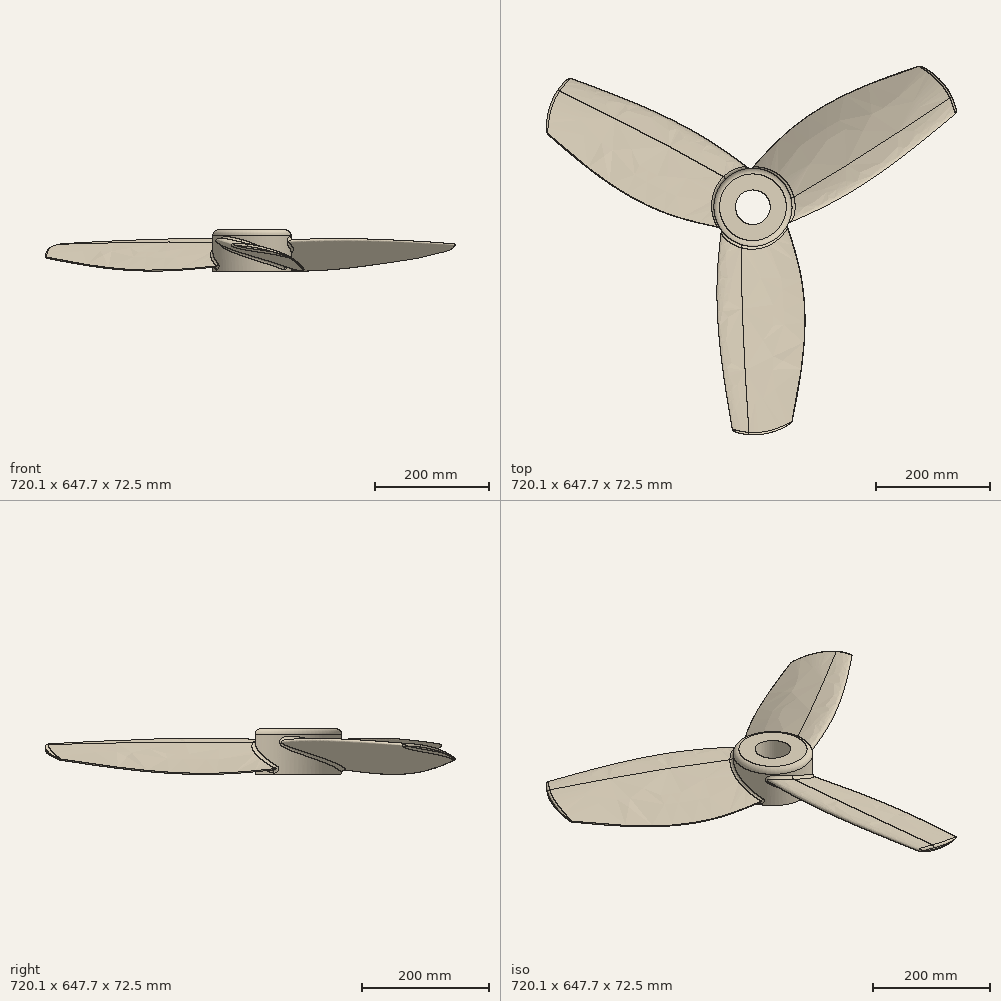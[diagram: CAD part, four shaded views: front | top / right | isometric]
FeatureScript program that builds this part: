
annotation { "Feature Type Name" : "Feature", "Feature Type Description" : "" }
export const myFeature = defineFeature(function(context is Context, id is Id, definition is map)
    precondition{}
    {
        {
            var Q0;
            Q0=qCreatedBy(makeId("Front.planeOp"),FACE);
            var sketch = newSketch(context, id + "F0", { "sketchPlane" : qUnion([Q0])});
            skLineSegment(sketch, "E0", {"start": v(-25.68, 10.16) * mm, "end": v(0, 0) * mm, "construction": true});
            skLineSegment(sketch, "E1", {"start": v(0, 0) * mm, "end": v(25.68, -10.16) * mm, "construction": true});
            skLineSegment(sketch, "E2", {"start": v(25.68, -10.16) * mm, "end": v(51.36, -20.31) * mm, "construction": true});
            skLineSegment(sketch, "E3", {"start": v(51.36, -20.31) * mm, "end": v(77.03, -30.47) * mm, "construction": true});
            skLineSegment(sketch, "E4", {"start": v(0, 0) * mm, "end": v(3.73, 9.44) * mm, "construction": true});
            skLineSegment(sketch, "E5", {"start": v(-25.68, 10.16) * mm, "end": v(-23.81, 14.88) * mm, "construction": true});
            skFitSpline(sketch, "E6", {"points": [v(-25.68, 10.16) * mm, v(3.73, 9.44) * mm, v(77.03, -30.47) * mm], "startDerivative": vector(15.03, 38) * mm, "endDerivative": vector(104.92, -93.69) * mm});
            skPoint(sketch, "E7", {"position": v(1.87, 4.72) * mm});
            skLineSegment(sketch, "E8", {"start": v(-23.81, 14.88) * mm, "end": v(1.87, 4.72) * mm, "construction": true});
            skLineSegment(sketch, "E9", {"start": v(0, 0) * mm, "end": v(-1.87, -4.72) * mm, "construction": true});
            skLineSegment(sketch, "E10", {"start": v(-25.68, 10.16) * mm, "end": v(-27.54, 5.44) * mm, "construction": true});
            skFitSpline(sketch, "E11", {"points": [v(-25.68, 10.16) * mm, v(-1.87, -4.72) * mm, v(77.03, -30.47) * mm], "startDerivative": vector(-15.23, -38.5) * mm, "endDerivative": vector(121.84, -48.19) * mm});
            skLineSegment(sketch, "E12", {"start": v(51.36, -20.31) * mm, "end": v(55.09, -10.87) * mm, "construction": true});
            skSolve(sketch);
        }
        {
            var Q0;
            Q0=qCreatedBy(makeId("Front.planeOp"),FACE);
            cPlane(context, id + "F1", {"entities" : qUnion([Q0]), "cplaneType" : CPlaneType.OFFSET, "offset" : 125 * mm, "width" : 150 * mm, "height" : 150 * mm});
        }
        {
            var Q0;
            Q0=qCreatedBy(id+"F1.planeOp",FACE);
            var sketch = newSketch(context, id + "F2", { "sketchPlane" : qUnion([Q0])});
            skLineSegment(sketch, "E13", {"start": v(-38.33, 14.06) * mm, "end": v(0, 0) * mm, "construction": true});
            skLineSegment(sketch, "E14", {"start": v(0, 0) * mm, "end": v(38.33, -14.06) * mm, "construction": true});
            skLineSegment(sketch, "E15", {"start": v(38.33, -14.06) * mm, "end": v(76.67, -28.12) * mm, "construction": true});
            skLineSegment(sketch, "E16", {"start": v(76.67, -28.12) * mm, "end": v(115, -42.17) * mm, "construction": true});
            skLineSegment(sketch, "E17", {"start": v(0, 0) * mm, "end": v(4.06, 11.06) * mm, "construction": true});
            skLineSegment(sketch, "E18", {"start": v(-38.33, 14.06) * mm, "end": v(-36.3, 19.59) * mm, "construction": true});
            skFitSpline(sketch, "E19", {"points": [v(-38.33, 14.06) * mm, v(4.06, 11.06) * mm, v(115, -42.17) * mm], "startDerivative": vector(16.44, 44.82) * mm, "endDerivative": vector(163.27, -119.63) * mm});
            skPoint(sketch, "E20", {"position": v(2.03, 5.53) * mm});
            skLineSegment(sketch, "E21", {"start": v(-36.3, 19.59) * mm, "end": v(2.03, 5.53) * mm, "construction": true});
            skLineSegment(sketch, "E22", {"start": v(0, 0) * mm, "end": v(-2.03, -5.53) * mm, "construction": true});
            skLineSegment(sketch, "E23", {"start": v(-38.33, 14.06) * mm, "end": v(-40.36, 8.53) * mm, "construction": true});
            skFitSpline(sketch, "E24", {"points": [v(-38.33, 14.06) * mm, v(-2.03, -5.53) * mm, v(115, -42.17) * mm], "startDerivative": vector(-16.57, -45.19) * mm, "endDerivative": vector(181.7, -66.64) * mm});
            skLineSegment(sketch, "E25", {"start": v(76.67, -28.12) * mm, "end": v(80.72, -17.06) * mm, "construction": true});
            skSolve(sketch);
        }
        {
            var Q0;
            Q0=qCreatedBy(makeId("Front.planeOp"),FACE);
            cPlane(context, id + "F3", {"entities" : qUnion([Q0]), "cplaneType" : CPlaneType.OFFSET, "offset" : 400 * mm, "width" : 150 * mm, "height" : 150 * mm});
        }
        {
            var Q0;
            Q0=qCreatedBy(id+"F3.planeOp",FACE);
            var sketch = newSketch(context, id + "F4", { "sketchPlane" : qUnion([Q0])});
            skLineSegment(sketch, "E26", {"start": v(-10.03, 5.14) * mm, "end": v(16.27, 0) * mm, "construction": true});
            skLineSegment(sketch, "E27", {"start": v(16.27, 0) * mm, "end": v(42.56, -5.14) * mm, "construction": true});
            skLineSegment(sketch, "E28", {"start": v(42.56, -5.14) * mm, "end": v(68.86, -10.28) * mm, "construction": true});
            skLineSegment(sketch, "E29", {"start": v(68.86, -10.28) * mm, "end": v(95.16, -15.42) * mm, "construction": true});
            skLineSegment(sketch, "E30", {"start": v(16.27, 0) * mm, "end": v(17.61, 6.9) * mm, "construction": true});
            skLineSegment(sketch, "E31", {"start": v(-10.03, 5.14) * mm, "end": v(-9.36, 8.59) * mm, "construction": true});
            skFitSpline(sketch, "E32", {"points": [v(-10.03, 5.14) * mm, v(17.61, 6.9) * mm, v(95.16, -15.42) * mm], "startDerivative": vector(5.47, 28.01) * mm, "endDerivative": vector(118.7, -57.28) * mm});
            skPoint(sketch, "E33", {"position": v(16.94, 3.45) * mm});
            skLineSegment(sketch, "E34", {"start": v(-9.36, 8.59) * mm, "end": v(16.94, 3.45) * mm, "construction": true});
            skLineSegment(sketch, "E35", {"start": v(16.27, 0) * mm, "end": v(15.6, -3.45) * mm, "construction": true});
            skLineSegment(sketch, "E36", {"start": v(-10.03, 5.14) * mm, "end": v(-10.7, 1.7) * mm, "construction": true});
            skFitSpline(sketch, "E37", {"points": [v(-10.03, 5.14) * mm, v(15.6, -3.45) * mm, v(95.16, -15.42) * mm], "startDerivative": vector(-5.51, -28.2) * mm, "endDerivative": vector(124.61, -24.36) * mm});
            skLineSegment(sketch, "E38", {"start": v(68.86, -10.28) * mm, "end": v(70.2, -3.38) * mm, "construction": true});
            skSolve(sketch);
        }
        {
            var Q0;
            Q0=qSketchRegion(id+"F0",true);
            var Q1;
            Q1=qSketchRegion(id+"F2",true);
            var Q2;
            Q2=qSketchRegion(id+"F4",true);
            var Q3;
            Q3=sQuery(id+"F0.wireOp",VERTEX,"E6.1.internal");
            var Q4;
            Q4=sQuery(id+"F2.wireOp",VERTEX,"E19.1.internal");
            var Q5;
            Q5=sQuery(id+"F4.wireOp",VERTEX,"E30.end");
            loft(context, id + "F5", {"sheetProfilesArray" : [{ "sheetProfileEntities" : qUnion([Q0]) }, { "sheetProfileEntities" : qUnion([Q1]) }, { "sheetProfileEntities" : qUnion([Q2]) }], "matchConnections" : true, "connections" : [{ "connectionEntities" : qUnion([Q3, Q4, Q5]), "connectionEdgeQueries" : qUnion([]), "connectionEdgeParameters" : [] }]});
        }
        {
            var Q0;
            Q0=qCreatedBy(makeId("Top.planeOp"),FACE);
            var sketch = newSketch(context, id + "F6", { "sketchPlane" : qUnion([Q0])});
            skFitSpline(sketch, "E39", {"points": [v(-55.98, -360.47) * mm, v(39.38, -398.87) * mm, v(142.8, -333.19) * mm], "startDerivative": vector(111.22, -150.8) * mm, "endDerivative": vector(54.24, 145.78) * mm});
            skLineSegment(sketch, "E40", {"start": v(-55.98, -360.47) * mm, "end": v(-55.98, -458.75) * mm});
            skLineSegment(sketch, "E41", {"start": v(142.8, -333.19) * mm, "end": v(142.8, -458.75) * mm});
            skLineSegment(sketch, "E42", {"start": v(142.8, -458.75) * mm, "end": v(-55.98, -458.75) * mm});
            skSolve(sketch);
        }
        {
            var Q0;
            Q0=qSketchRegion(id+"F6",true);
            extrude(context, id + "F7", {"entities" : qUnion([Q0]), "operationType" : NewBodyOperationType.REMOVE, "endBound" : BoundingType.SYMMETRIC, "oppositeDirection" : true, "depth" : 40.17 * mm, "offsetDistance" : 25 * mm});
        }
        {
            var Q0;
            Q0=makeQuery(id+"F5.opLoft","SWEPT_EDGE",EDGE,{"disambiguationData":[OSD([sQuery(id+"F2.wireOp",EDGE,"E19"),sQuery(id+"F2.wireOp",EDGE,"E24"),sQuery(id+"F4.wireOp",EDGE,"E32"),sQuery(id+"F4.wireOp",EDGE,"E37")])]});
            fillet(context, id + "F8", {"entities" : qUnion([Q0]), "radius" : 1 * mm, "tangentPropagation" : true, "allowEdgeOverflow" : false});
        }
        {
            var Q0;
            Q0=makeQuery(id+"F7.boolean.opBoolean","COPY",FACE,{"derivedFrom":makeQuery(id+"F7.opExtrude","SWEPT_FACE",FACE,{"disambiguationData":[OSD([sQuery(id+"F6.wireOp",EDGE,"E39")])]})});
            fillet(context, id + "F9", {"entities" : qUnion([Q0]), "radius" : 4 * mm, "tangentPropagation" : true, "allowEdgeOverflow" : false});
        }
        {
            var Q0;
            Q0=qCreatedBy(makeId("Top.planeOp"),FACE);
            var sketch = newSketch(context, id + "F10", { "sketchPlane" : qUnion([Q0])});
            skCircle(sketch, "E43", {"center": v(24.35, 0) * mm, "radius": 68.6 * mm});
            skSolve(sketch);
        }
        {
            var Q0;
            Q0=qSketchRegion(id+"F10",true);
            extrude(context, id + "F11", {"entities" : qUnion([Q0]), "depth" : 32.31 * mm, "hasSecondDirection" : true, "secondDirectionOppositeDirection" : true, "secondDirectionDepth" : 40 * mm});
        }
        {
            var Q0;
            Q0=makeQuery(id+"F5.opLoft","SWEPT_BODY",BODY,{"disambiguationData":[OSD([makeQuery(id+"F0.imprint","IMPRINT",FACE,{"disambiguationData":[TD([[makeQuery(id+"F0.imprint","IMPRINT",EDGE,{"derivedFrom":sQuery(id+"F0.wireOp",EDGE,"E6")}),-1.0]])]}),sQuery(id+"F2.wireOp",EDGE,"E24"),makeQuery(id+"F4.imprint","IMPRINT",FACE,{"disambiguationData":[TD([[makeQuery(id+"F4.imprint","IMPRINT",EDGE,{"derivedFrom":sQuery(id+"F4.wireOp",EDGE,"E32")}),-1.0]])]})])]});
            var Q1;
            Q1=makeQuery(id+"F11.opExtrude","SWEPT_FACE",FACE,{"disambiguationData":[OSD([sQuery(id+"F10.wireOp",EDGE,"E43")])]});
            circularPattern(context, id + "F12", {"entities" : qUnion([Q0]), "axis" : qUnion([Q1]), "angle" : 360 * degree, "instanceCount" : 3, "equalSpace" : true});
        }
        {
            var Q0;
            Q0=makeQuery(id+"F12.opPattern","COPY",BODY,{"derivedFrom":makeQuery(id+"F5.opLoft","SWEPT_BODY",BODY,{"disambiguationData":[OSD([makeQuery(id+"F0.imprint","IMPRINT",FACE,{"disambiguationData":[TD([[makeQuery(id+"F0.imprint","IMPRINT",EDGE,{"derivedFrom":sQuery(id+"F0.wireOp",EDGE,"E6")}),-1.0]])]}),sQuery(id+"F2.wireOp",EDGE,"E24"),makeQuery(id+"F4.imprint","IMPRINT",FACE,{"disambiguationData":[TD([[makeQuery(id+"F4.imprint","IMPRINT",EDGE,{"derivedFrom":sQuery(id+"F4.wireOp",EDGE,"E32")}),-1.0]])]})])]}),"instanceName":"2"});
            var Q1;
            Q1=makeQuery(id+"F5.opLoft","SWEPT_BODY",BODY,{"disambiguationData":[OSD([makeQuery(id+"F0.imprint","IMPRINT",FACE,{"disambiguationData":[TD([[makeQuery(id+"F0.imprint","IMPRINT",EDGE,{"derivedFrom":sQuery(id+"F0.wireOp",EDGE,"E6")}),-1.0]])]}),sQuery(id+"F2.wireOp",EDGE,"E24"),makeQuery(id+"F4.imprint","IMPRINT",FACE,{"disambiguationData":[TD([[makeQuery(id+"F4.imprint","IMPRINT",EDGE,{"derivedFrom":sQuery(id+"F4.wireOp",EDGE,"E32")}),-1.0]])]})])]});
            var Q2;
            Q2=makeQuery(id+"F11.opExtrude","SWEPT_BODY",BODY,{"disambiguationData":[OSD([sQuery(id+"F10.wireOp",EDGE,"E43")])]});
            var Q3;
            Q3=makeQuery(id+"F12.opPattern","COPY",BODY,{"derivedFrom":makeQuery(id+"F5.opLoft","SWEPT_BODY",BODY,{"disambiguationData":[OSD([makeQuery(id+"F0.imprint","IMPRINT",FACE,{"disambiguationData":[TD([[makeQuery(id+"F0.imprint","IMPRINT",EDGE,{"derivedFrom":sQuery(id+"F0.wireOp",EDGE,"E6")}),-1.0]])]}),sQuery(id+"F2.wireOp",EDGE,"E24"),makeQuery(id+"F4.imprint","IMPRINT",FACE,{"disambiguationData":[TD([[makeQuery(id+"F4.imprint","IMPRINT",EDGE,{"derivedFrom":sQuery(id+"F4.wireOp",EDGE,"E32")}),-1.0]])]})])]}),"instanceName":"1"});
            var Q4;
            Q4=makeQuery(id+"F12.opPattern","COPY",BODY,{"derivedFrom":makeQuery(id+"F5.opLoft","SWEPT_BODY",BODY,{"disambiguationData":[OSD([makeQuery(id+"F0.imprint","IMPRINT",FACE,{"disambiguationData":[TD([[makeQuery(id+"F0.imprint","IMPRINT",EDGE,{"derivedFrom":sQuery(id+"F0.wireOp",EDGE,"E6")}),-1.0]])]}),sQuery(id+"F2.wireOp",EDGE,"E24"),makeQuery(id+"F4.imprint","IMPRINT",FACE,{"disambiguationData":[TD([[makeQuery(id+"F4.imprint","IMPRINT",EDGE,{"derivedFrom":sQuery(id+"F4.wireOp",EDGE,"E32")}),-1.0]])]})])]}),"instanceName":"4"});
            var Q5;
            Q5=makeQuery(id+"F12.opPattern","COPY",BODY,{"derivedFrom":makeQuery(id+"F5.opLoft","SWEPT_BODY",BODY,{"disambiguationData":[OSD([makeQuery(id+"F0.imprint","IMPRINT",FACE,{"disambiguationData":[TD([[makeQuery(id+"F0.imprint","IMPRINT",EDGE,{"derivedFrom":sQuery(id+"F0.wireOp",EDGE,"E6")}),-1.0]])]}),sQuery(id+"F2.wireOp",EDGE,"E24"),makeQuery(id+"F4.imprint","IMPRINT",FACE,{"disambiguationData":[TD([[makeQuery(id+"F4.imprint","IMPRINT",EDGE,{"derivedFrom":sQuery(id+"F4.wireOp",EDGE,"E32")}),-1.0]])]})])]}),"instanceName":"3"});
            booleanBodies(context, id + "F13", {"operationType" : BooleanOperationType.UNION, "tools" : qUnion([Q0, Q1, Q2, Q3, Q4, Q5])});
        }
        {
            var Q0;
            Q0=makeQuery(id+"F11.opExtrude","CAP_FACE",FACE,{"disambiguationData":[OSD([sQuery(id+"F10.wireOp",EDGE,"E43")])],"isStart":false});
            var sketch = newSketch(context, id + "F14", { "sketchPlane" : qUnion([Q0])});
            skCircle(sketch, "E44", {"center": v(24.35, 0) * mm, "radius": 30.45 * mm});
            skSolve(sketch);
        }
        {
            var Q0;
            Q0=qSketchRegion(id+"F14",true);
            var Q1;
            Q1 = qSketchRegion(id + "F14", true);
            var Q2;
            Q2 = qSketchRegion(id + "F14", true);
            extrude(context, id + "F15", {"entities" : qUnion([Q0, Q1, Q2]), "operationType" : NewBodyOperationType.REMOVE, "endBound" : BoundingType.THROUGH_ALL, "oppositeDirection" : true, "depth" : 25 * mm, "offsetDistance" : 25 * mm});
        }
        {
            var Q0;
            {var subQ0=sQuery(id+"F0.wireOp",VERTEX,"E6.1.internal");var subQ1=sQuery(id+"F0.wireOp",EDGE,"E6");var subQ2=sQuery(id+"F0.wireOp",EDGE,"E11");var subQ3=sQuery(id+"F2.wireOp",VERTEX,"E19.1.internal");var subQ4=sQuery(id+"F2.wireOp",EDGE,"E19");var subQ5=sQuery(id+"F2.wireOp",EDGE,"E24");Q0=makeQuery(id+"F13.opBoolean","INTERSECT",EDGE,{"derivedFrom":[makeQuery(id+"F11.opExtrude","SWEPT_FACE",FACE,{"disambiguationData":[OSD([sQuery(id+"F10.wireOp",EDGE,"E43")])]}),makeQuery(id+"F12.opPattern","COPY",FACE,{"derivedFrom":makeQuery(id+"F5.opLoft","SWEPT_FACE",FACE,{"disambiguationData":[OSD([subQ0,subQ1,subQ2,subQ3,subQ4,subQ5]),TDD([subQ0,makeQuery(id+"F0.imprint","INTERSECT",VERTEX,{"disambiguationData":[OD(0.0)],"derivedFrom":[subQ1,subQ2]}),makeQuery(id+"F0.imprint","IMPRINT",EDGE,{"derivedFrom":subQ1}),subQ3,makeQuery(id+"F2.imprint","INTERSECT",VERTEX,{"disambiguationData":[OD(0.0)],"derivedFrom":[subQ4,subQ5]}),makeQuery(id+"F2.imprint","IMPRINT",EDGE,{"derivedFrom":subQ4})])]}),"instanceName":"2"})]});}
            var Q1;
            {var subQ0=sQuery(id+"F0.wireOp",VERTEX,"E6.1.internal");var subQ1=sQuery(id+"F0.wireOp",EDGE,"E6");var subQ2=sQuery(id+"F0.wireOp",EDGE,"E11");var subQ3=sQuery(id+"F2.wireOp",VERTEX,"E19.1.internal");var subQ4=sQuery(id+"F2.wireOp",EDGE,"E19");var subQ5=sQuery(id+"F2.wireOp",EDGE,"E24");Q1=makeQuery(id+"F13.opBoolean","INTERSECT",EDGE,{"derivedFrom":[makeQuery(id+"F5.opLoft","SWEPT_FACE",FACE,{"disambiguationData":[OSD([subQ0,subQ1,subQ2,subQ3,subQ4,subQ5]),TDD([subQ0,makeQuery(id+"F0.imprint","INTERSECT",VERTEX,{"disambiguationData":[OD(1.0)],"derivedFrom":[subQ1,subQ2]}),makeQuery(id+"F0.imprint","IMPRINT",EDGE,{"derivedFrom":subQ1}),subQ3,makeQuery(id+"F2.imprint","INTERSECT",VERTEX,{"disambiguationData":[OD(1.0)],"derivedFrom":[subQ4,subQ5]}),makeQuery(id+"F2.imprint","IMPRINT",EDGE,{"derivedFrom":subQ4})])]}),makeQuery(id+"F11.opExtrude","SWEPT_FACE",FACE,{"disambiguationData":[OSD([sQuery(id+"F10.wireOp",EDGE,"E43")])]})]});}
            var Q2;
            {var subQ0=sQuery(id+"F0.wireOp",VERTEX,"E6.1.internal");var subQ1=sQuery(id+"F0.wireOp",EDGE,"E6");var subQ2=sQuery(id+"F0.wireOp",EDGE,"E11");var subQ3=sQuery(id+"F2.wireOp",VERTEX,"E19.1.internal");var subQ4=sQuery(id+"F2.wireOp",EDGE,"E19");var subQ5=sQuery(id+"F2.wireOp",EDGE,"E24");Q2=makeQuery(id+"F13.opBoolean","INTERSECT",EDGE,{"derivedFrom":[makeQuery(id+"F11.opExtrude","SWEPT_FACE",FACE,{"disambiguationData":[OSD([sQuery(id+"F10.wireOp",EDGE,"E43")])]}),makeQuery(id+"F12.opPattern","COPY",FACE,{"derivedFrom":makeQuery(id+"F5.opLoft","SWEPT_FACE",FACE,{"disambiguationData":[OSD([subQ0,subQ1,subQ2,subQ3,subQ4,subQ5]),TDD([subQ0,makeQuery(id+"F0.imprint","INTERSECT",VERTEX,{"disambiguationData":[OD(1.0)],"derivedFrom":[subQ1,subQ2]}),makeQuery(id+"F0.imprint","IMPRINT",EDGE,{"derivedFrom":subQ1}),subQ3,makeQuery(id+"F2.imprint","INTERSECT",VERTEX,{"disambiguationData":[OD(1.0)],"derivedFrom":[subQ4,subQ5]}),makeQuery(id+"F2.imprint","IMPRINT",EDGE,{"derivedFrom":subQ4})])]}),"instanceName":"1"})]});}
            var Q3;
            {var subQ0=sQuery(id+"F0.wireOp",VERTEX,"E6.1.internal");var subQ1=sQuery(id+"F0.wireOp",EDGE,"E6");var subQ2=sQuery(id+"F0.wireOp",EDGE,"E11");var subQ3=sQuery(id+"F2.wireOp",VERTEX,"E19.1.internal");var subQ4=sQuery(id+"F2.wireOp",EDGE,"E19");var subQ5=sQuery(id+"F2.wireOp",EDGE,"E24");Q3=makeQuery(id+"F13.opBoolean","INTERSECT",EDGE,{"derivedFrom":[makeQuery(id+"F11.opExtrude","SWEPT_FACE",FACE,{"disambiguationData":[OSD([sQuery(id+"F10.wireOp",EDGE,"E43")])]}),makeQuery(id+"F12.opPattern","COPY",FACE,{"derivedFrom":makeQuery(id+"F5.opLoft","SWEPT_FACE",FACE,{"disambiguationData":[OSD([subQ0,subQ1,subQ2,subQ3,subQ4,subQ5]),TDD([subQ0,makeQuery(id+"F0.imprint","INTERSECT",VERTEX,{"disambiguationData":[OD(1.0)],"derivedFrom":[subQ1,subQ2]}),makeQuery(id+"F0.imprint","IMPRINT",EDGE,{"derivedFrom":subQ1}),subQ3,makeQuery(id+"F2.imprint","INTERSECT",VERTEX,{"disambiguationData":[OD(1.0)],"derivedFrom":[subQ4,subQ5]}),makeQuery(id+"F2.imprint","IMPRINT",EDGE,{"derivedFrom":subQ4})])]}),"instanceName":"4"})]});}
            var Q4;
            {var subQ0=sQuery(id+"F0.wireOp",VERTEX,"E6.1.internal");var subQ1=sQuery(id+"F0.wireOp",EDGE,"E6");var subQ2=sQuery(id+"F0.wireOp",EDGE,"E11");var subQ3=sQuery(id+"F2.wireOp",VERTEX,"E19.1.internal");var subQ4=sQuery(id+"F2.wireOp",EDGE,"E19");var subQ5=sQuery(id+"F2.wireOp",EDGE,"E24");Q4=makeQuery(id+"F13.opBoolean","INTERSECT",EDGE,{"derivedFrom":[makeQuery(id+"F11.opExtrude","SWEPT_FACE",FACE,{"disambiguationData":[OSD([sQuery(id+"F10.wireOp",EDGE,"E43")])]}),makeQuery(id+"F12.opPattern","COPY",FACE,{"derivedFrom":makeQuery(id+"F5.opLoft","SWEPT_FACE",FACE,{"disambiguationData":[OSD([subQ0,subQ1,subQ2,subQ3,subQ4,subQ5]),TDD([subQ0,makeQuery(id+"F0.imprint","INTERSECT",VERTEX,{"disambiguationData":[OD(0.0)],"derivedFrom":[subQ1,subQ2]}),makeQuery(id+"F0.imprint","IMPRINT",EDGE,{"derivedFrom":subQ1}),subQ3,makeQuery(id+"F2.imprint","INTERSECT",VERTEX,{"disambiguationData":[OD(0.0)],"derivedFrom":[subQ4,subQ5]}),makeQuery(id+"F2.imprint","IMPRINT",EDGE,{"derivedFrom":subQ4})])]}),"instanceName":"3"})]});}
            fillet(context, id + "F16", {"entities" : qUnion([Q0, Q1, Q2, Q3, Q4]), "radius" : 5 * mm, "tangentPropagation" : true, "allowEdgeOverflow" : false});
        }
        {
            var Q0;
            Q0=makeQuery(id+"F11.opExtrude","CAP_EDGE",EDGE,{"disambiguationData":[OSD([sQuery(id+"F10.wireOp",EDGE,"E43")])],"isStart":false});
            fillet(context, id + "F17", {"entities" : qUnion([Q0]), "radius" : 10 * mm, "tangentPropagation" : true, "allowEdgeOverflow" : false});
        }
    });
